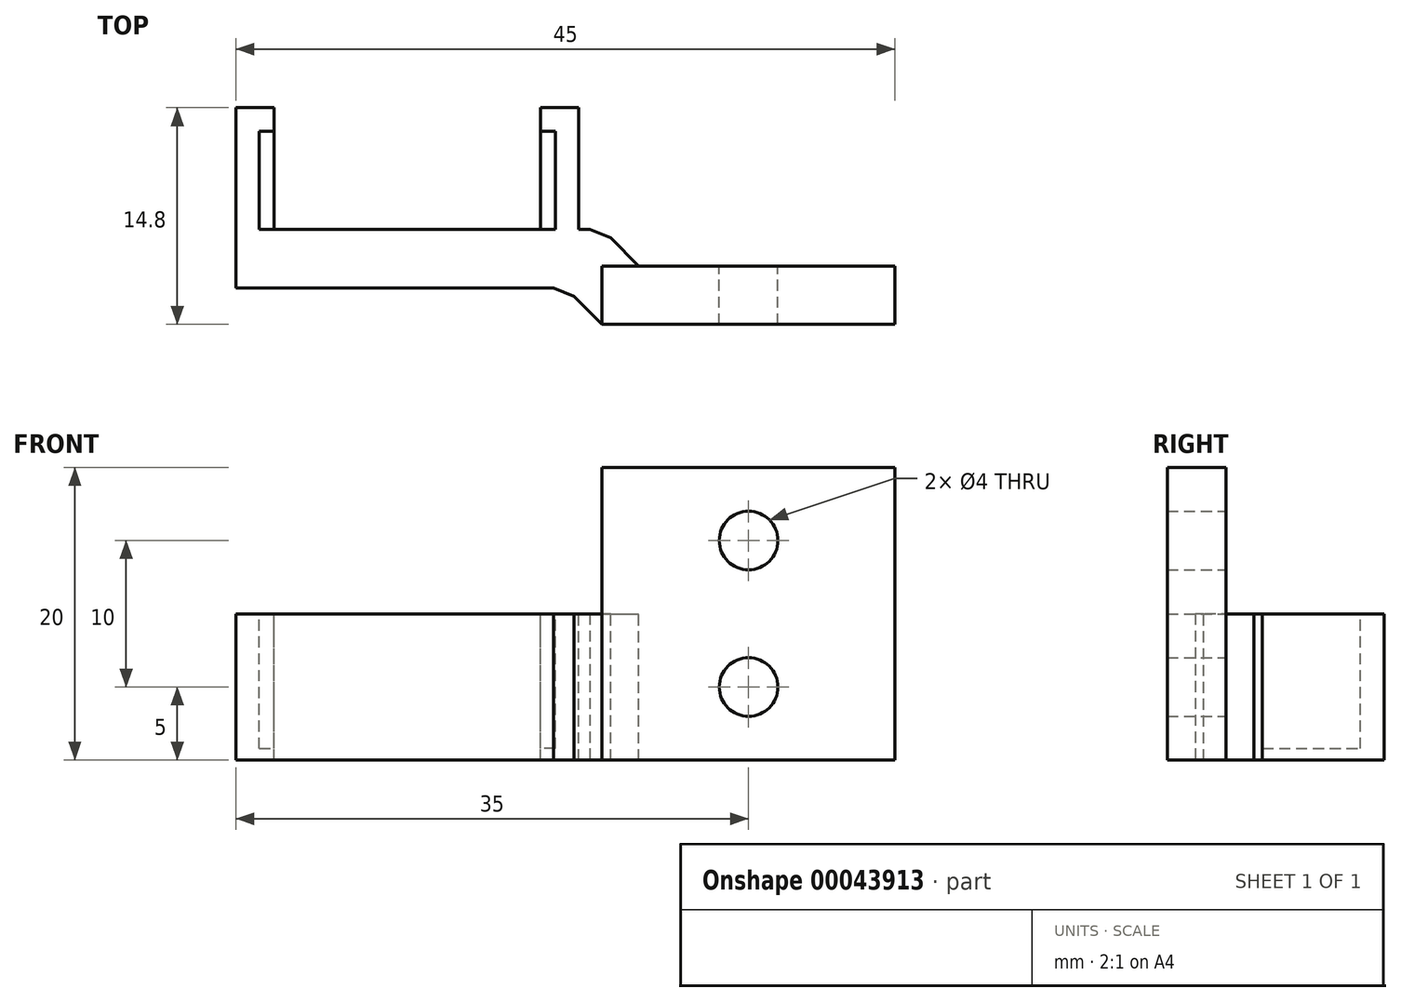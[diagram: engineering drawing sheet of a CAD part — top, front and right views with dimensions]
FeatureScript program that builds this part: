
annotation { "Feature Type Name" : "Feature", "Feature Type Description" : "" }
export const myFeature = defineFeature(function(context is Context, id is Id, definition is map)
    precondition{}
    {
        {
            var Q0;
            Q0=qCreatedBy(makeId("Top.planeOp"),FACE);
            var sketch = newSketch(context, id + "F0", { "sketchPlane" : qUnion([Q0])});
            skLineSegment(sketch, "E0", {"start": v(-10.1, -3.35) * mm, "end": v(-9.1, -3.35) * mm});
            skLineSegment(sketch, "E1", {"start": v(-9.1, -3.35) * mm, "end": v(-9.1, -4.95) * mm});
            skLineSegment(sketch, "E2", {"start": v(-9.1, -4.95) * mm, "end": v(-11.7, -4.95) * mm});
            skLineSegment(sketch, "E3", {"start": v(-11.7, -4.95) * mm, "end": v(-11.7, 7.35) * mm});
            skLineSegment(sketch, "E4", {"start": v(-11.7, 7.35) * mm, "end": v(11.7, 7.35) * mm});
            skLineSegment(sketch, "E5", {"start": v(11.7, 7.35) * mm, "end": v(11.7, -4.95) * mm});
            skLineSegment(sketch, "E6", {"start": v(11.7, -4.95) * mm, "end": v(9.1, -4.95) * mm});
            skLineSegment(sketch, "E7", {"start": v(9.1, -4.95) * mm, "end": v(9.1, -3.35) * mm});
            skLineSegment(sketch, "E8", {"start": v(9.1, -3.35) * mm, "end": v(10.1, -3.35) * mm});
            skLineSegment(sketch, "E9", {"start": v(10.1, -3.35) * mm, "end": v(10.1, 3.35) * mm});
            skLineSegment(sketch, "E10", {"start": v(10.1, 3.35) * mm, "end": v(-10.1, 3.35) * mm});
            skLineSegment(sketch, "E11", {"start": v(-10.1, 3.35) * mm, "end": v(-10.1, -3.35) * mm});
            skLineSegment(sketch, "E12", {"start": v(11.7, 7.35) * mm, "end": v(33.3, 7.35) * mm});
            skLineSegment(sketch, "E13", {"start": v(33.3, 7.35) * mm, "end": v(33.3, 3.35) * mm});
            skLineSegment(sketch, "E14", {"start": v(33.3, 3.35) * mm, "end": v(11.7, 3.35) * mm});
            skLineSegment(sketch, "E15", {"start": v(13.3, 7.35) * mm, "end": v(13.3, 3.35) * mm});
            skLineSegment(sketch, "E16", {"start": v(13.3, 7.35) * mm, "end": v(13.3, 9.85) * mm});
            skLineSegment(sketch, "E17", {"start": v(13.3, 9.85) * mm, "end": v(33.3, 9.85) * mm});
            skLineSegment(sketch, "E18", {"start": v(33.3, 9.85) * mm, "end": v(33.3, 7.35) * mm});
            skLineSegment(sketch, "E19", {"start": v(13.3, 5.85) * mm, "end": v(33.3, 5.85) * mm});
            skLineSegment(sketch, "E20", {"start": v(13.3, 9.85) * mm, "end": v(10.8, 7.35) * mm});
            skLineSegment(sketch, "E21", {"start": v(13.3, 3.35) * mm, "end": v(15.8, 5.85) * mm});
            skSolve(sketch);
        }
        {
            var Q0;
            Q0=makeQuery(id+"F0.imprint","IMPRINT",FACE,{"disambiguationData":[TD([[makeQuery(id+"F0.imprint","IMPRINT",EDGE,{"derivedFrom":sQuery(id+"F0.wireOp",EDGE,"E0")}),-1.0]])]});
            var Q1;
            {var subQ0=sQuery(id+"F0.wireOp",EDGE,"E15");Q1=makeQuery(id+"F0.imprint","IMPRINT",FACE,{"disambiguationData":[TD([[makeQuery(id+"F0.imprint","IMPRINT",EDGE,{"derivedFrom":subQ0}),-1.0]])]});}
            var Q2;
            {var subQ1=sQuery(id+"F0.wireOp",EDGE,"E12");Q2=makeQuery(id+"F0.imprint","IMPRINT",FACE,{"disambiguationData":[TD([[makeQuery(id+"F0.imprint","IMPRINT",EDGE,{"derivedFrom":subQ1}),1.0]])]});}
            var Q3;
            {var subQ2=sQuery(id+"F0.wireOp",EDGE,"E15");Q3=makeQuery(id+"F0.imprint","IMPRINT",FACE,{"disambiguationData":[TD([[makeQuery(id+"F0.imprint","IMPRINT",EDGE,{"derivedFrom":subQ2}),1.0]])]});}
            extrude(context, id + "F1", {"entities" : qUnion([Q0, Q1, Q2, Q3]), "depth" : 9.2 * mm});
        }
        {
            var Q0;
            {var subQ0=sQuery(id+"F0.wireOp",EDGE,"E19");Q0=makeQuery(id+"F0.imprint","IMPRINT",FACE,{"disambiguationData":[TD([[makeQuery(id+"F0.imprint","IMPRINT",EDGE,{"derivedFrom":subQ0}),1.0]])]});}
            var Q1;
            {var subQ1=sQuery(id+"F0.wireOp",EDGE,"E16");Q1=makeQuery(id+"F0.imprint","IMPRINT",FACE,{"disambiguationData":[TD([[makeQuery(id+"F0.imprint","IMPRINT",EDGE,{"derivedFrom":subQ1}),-1.0]])]});}
            extrude(context, id + "F2", {"entities" : qUnion([Q0, Q1]), "operationType" : NewBodyOperationType.ADD, "endBound" : BoundingType.SYMMETRIC, "depth" : 20 * mm});
        }
        {
            var Q0;
            Q0=makeQuery(id+"F2.opExtrude","SWEPT_FACE",FACE,{"disambiguationData":[OSD([sQuery(id+"F0.wireOp",EDGE,"E19")])]});
            var sketch = newSketch(context, id + "F3", { "sketchPlane" : qUnion([Q0])});
            skCircle(sketch, "E22", {"center": v(23.3, 5) * mm, "radius": 2 * mm});
            skCircle(sketch, "E23", {"center": v(23.3, -5) * mm, "radius": 2 * mm});
            skSolve(sketch);
        }
        {
            var Q0;
            Q0=makeQuery(id+"F3.imprint","IMPRINT",FACE,{"disambiguationData":[TD([[makeQuery(id+"F3.imprint","IMPRINT",EDGE,{"derivedFrom":sQuery(id+"F3.wireOp",EDGE,"E22")}),1.0]])]});
            var Q1;
            Q1=makeQuery(id+"F3.imprint","IMPRINT",FACE,{"disambiguationData":[TD([[makeQuery(id+"F3.imprint","IMPRINT",EDGE,{"derivedFrom":sQuery(id+"F3.wireOp",EDGE,"E23")}),1.0]])]});
            extrude(context, id + "F4", {"entities" : qUnion([Q0, Q1]), "operationType" : NewBodyOperationType.REMOVE, "oppositeDirection" : true, "depth" : 25 * mm});
        }
        {
            var Q0;
            Q0=makeQuery(id+"F1.opExtrude","CAP_FACE",FACE,{"disambiguationData":[OSD([sQuery(id+"F0.wireOp",EDGE,"E0"),sQuery(id+"F0.wireOp",EDGE,"E1"),sQuery(id+"F0.wireOp",EDGE,"E2"),sQuery(id+"F0.wireOp",EDGE,"E3"),sQuery(id+"F0.wireOp",EDGE,"E4"),sQuery(id+"F0.wireOp",EDGE,"E5"),sQuery(id+"F0.wireOp",EDGE,"E6"),sQuery(id+"F0.wireOp",EDGE,"E7"),sQuery(id+"F0.wireOp",EDGE,"E8"),sQuery(id+"F0.wireOp",EDGE,"E9"),sQuery(id+"F0.wireOp",EDGE,"E10"),sQuery(id+"F0.wireOp",EDGE,"E11"),sQuery(id+"F0.wireOp",EDGE,"E12"),sQuery(id+"F0.wireOp",EDGE,"E14"),sQuery(id+"F0.wireOp",EDGE,"E15")])],"isStart":false});
            var sketch = newSketch(context, id + "F5", { "sketchPlane" : qUnion([Q0])});
            skLineSegment(sketch, "E24", {"start": v(-9.1, -3.35) * mm, "end": v(-9.1, 3.35) * mm});
            skLineSegment(sketch, "E25", {"start": v(9.1, -3.35) * mm, "end": v(9.1, 3.35) * mm});
            skSolve(sketch);
        }
        {
            var Q0;
            Q0=makeQuery(id+"F5.imprint","IMPRINT",FACE,{"disambiguationData":[TD([[makeQuery(id+"F5.imprint","IMPRINT",EDGE,{"derivedFrom":makeQuery(id+"F1.opExtrude","CAP_EDGE",EDGE,{"disambiguationData":[OSD([sQuery(id+"F0.wireOp",EDGE,"E0")])],"isStart":false})}),-1.0]])]});
            var Q1;
            {var subQ1=sQuery(id+"F5.wireOp",EDGE,"E24");Q1=makeQuery(id+"F5.imprint","IMPRINT",FACE,{"disambiguationData":[TD([[makeQuery(id+"F5.imprint","IMPRINT",EDGE,{"derivedFrom":subQ1}),1.0]])]});}
            var Q2;
            {var subQ1=sQuery(id+"F5.wireOp",EDGE,"E25");Q2=makeQuery(id+"F5.imprint","IMPRINT",FACE,{"disambiguationData":[TD([[makeQuery(id+"F5.imprint","IMPRINT",EDGE,{"derivedFrom":subQ1}),-1.0]])]});}
            var Q3;
            Q3=makeQuery(id+"F2.opExtrude","CAP_FACE",FACE,{"disambiguationData":[OSD([sQuery(id+"F0.wireOp",EDGE,"E13"),sQuery(id+"F0.wireOp",EDGE,"E15"),sQuery(id+"F0.wireOp",EDGE,"E16"),sQuery(id+"F0.wireOp",EDGE,"E17"),sQuery(id+"F0.wireOp",EDGE,"E18"),sQuery(id+"F0.wireOp",EDGE,"E19")])],"isStart":false});
            extrude(context, id + "F6", {"entities" : qUnion([Q0, Q1, Q2]), "operationType" : NewBodyOperationType.ADD, "endBound" : BoundingType.UP_TO_SURFACE, "endBoundEntityFace" : qUnion([Q3]), "depth" : 1 * mm});
        }
        {
            var Q0;
            {var subQ0=sQuery(id+"F0.wireOp",EDGE,"E4");var subQ1=sQuery(id+"F0.wireOp",EDGE,"E20");Q0=makeQuery(id+"F6.boolean.opBoolean","MERGE",EDGE,{"derivedFrom":[makeQuery(id+"F1.opExtrude","SWEPT_EDGE",EDGE,{"disambiguationData":[OSD([subQ0,subQ1])]}),makeQuery(id+"F6.opExtrude","SWEPT_EDGE",EDGE,{"disambiguationData":[OSD([subQ0,subQ1])]})]});}
            var Q1;
            {var subQ0=sQuery(id+"F0.wireOp",EDGE,"E14");var subQ1=sQuery(id+"F0.wireOp",EDGE,"E21");Q1=makeQuery(id+"F6.boolean.opBoolean","MERGE",EDGE,{"derivedFrom":[makeQuery(id+"F1.opExtrude","SWEPT_EDGE",EDGE,{"disambiguationData":[OSD([subQ0,sQuery(id+"F0.wireOp",EDGE,"E15"),subQ1])]}),makeQuery(id+"F6.opExtrude","SWEPT_EDGE",EDGE,{"disambiguationData":[OSD([subQ0,subQ1])]})]});}
            chamfer(context, id + "F7", {"entities" : qUnion([Q0, Q1]), "width" : 2 * mm, "tangentPropagation" : true});
        }
        {
            var Q0;
            Q0=makeQuery(id+"F1.opExtrude","SWEPT_BODY",BODY,{"disambiguationData":[OSD([sQuery(id+"F0.wireOp",EDGE,"E0"),sQuery(id+"F0.wireOp",EDGE,"E1"),sQuery(id+"F0.wireOp",EDGE,"E2"),sQuery(id+"F0.wireOp",EDGE,"E3"),sQuery(id+"F0.wireOp",EDGE,"E4"),sQuery(id+"F0.wireOp",EDGE,"E5"),sQuery(id+"F0.wireOp",EDGE,"E6"),sQuery(id+"F0.wireOp",EDGE,"E7"),sQuery(id+"F0.wireOp",EDGE,"E8"),sQuery(id+"F0.wireOp",EDGE,"E9"),sQuery(id+"F0.wireOp",EDGE,"E10"),sQuery(id+"F0.wireOp",EDGE,"E11"),sQuery(id+"F0.wireOp",EDGE,"E12"),sQuery(id+"F0.wireOp",EDGE,"E14"),sQuery(id+"F0.wireOp",EDGE,"E15"),sQuery(id+"F0.wireOp",EDGE,"E17"),sQuery(id+"F0.wireOp",EDGE,"E18"),sQuery(id+"F0.wireOp",EDGE,"E19"),sQuery(id+"F0.wireOp",EDGE,"E20"),sQuery(id+"F0.wireOp",EDGE,"E21")])]});
            var Q1;
            Q1=makeQuery(id+"F2.opExtrude","CAP_EDGE",EDGE,{"disambiguationData":[OSD([sQuery(id+"F0.wireOp",EDGE,"E19")])],"isStart":false});
            transform(context, id + "F8", {"entities" : qUnion([Q0]), "transformType" : TransformType.ROTATION, "transformAxis" : qUnion([Q1]), "angle" : 180 * degree, "makeCopy" : false});
        }
    });
